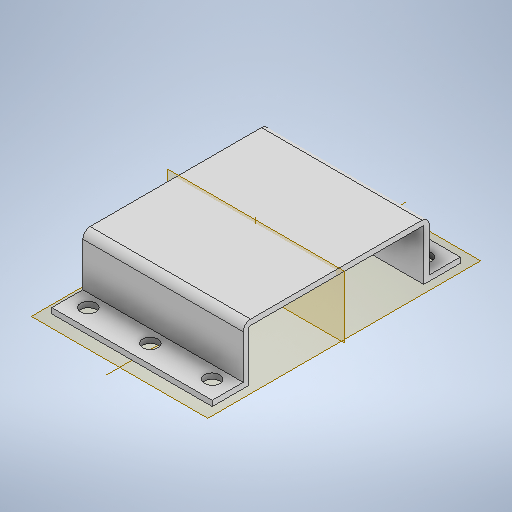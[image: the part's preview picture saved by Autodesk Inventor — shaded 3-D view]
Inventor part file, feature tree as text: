
AUTODESK INVENTOR PART (.ipt)
format: ipt  version: 2025 (Build 290162000, 162)  size: 264,192 bytes
history: native  units: mm
features: sketch x2, extrude x1, hole x1, mirror x1
ambient origin geometry x8: Origin, YZ Plane, XZ Plane, XY Plane, X Axis, Y Axis, Z Axis, Center Point
bodies: Solid1 (feature_tree)
feature tree (5):
  extrude  "Extrusion1"  Depth=1.5mm
  hole  "Hole1"  [1 undecoded]
  mirror  "Mirror1"
  sketch  "Sketch2"  dims[d0=10.0mm d1=1.5mm]
  sketch  "Sketch3"  dims[d2=8.5mm d4=14.0mm d5=24.0mm d6=1.5mm d7=2.0mm d8=44.0mm d9=0.0mm d10=5.0mm d12=17.0mm d14=5.0mm d15=4.2mm d16=6.0mm d17=4.0mm d18=2.0mm d19=90.0deg d20=8.0mm d21=20.594885mm d22=0.5mm d23=17.0mm d24=5.0mm]
note: 1 required parameter value undecoded (feature->parameter linkage not recoverable at this tier; creation-order binding heuristic only, values carry confidence <= 0.55)
